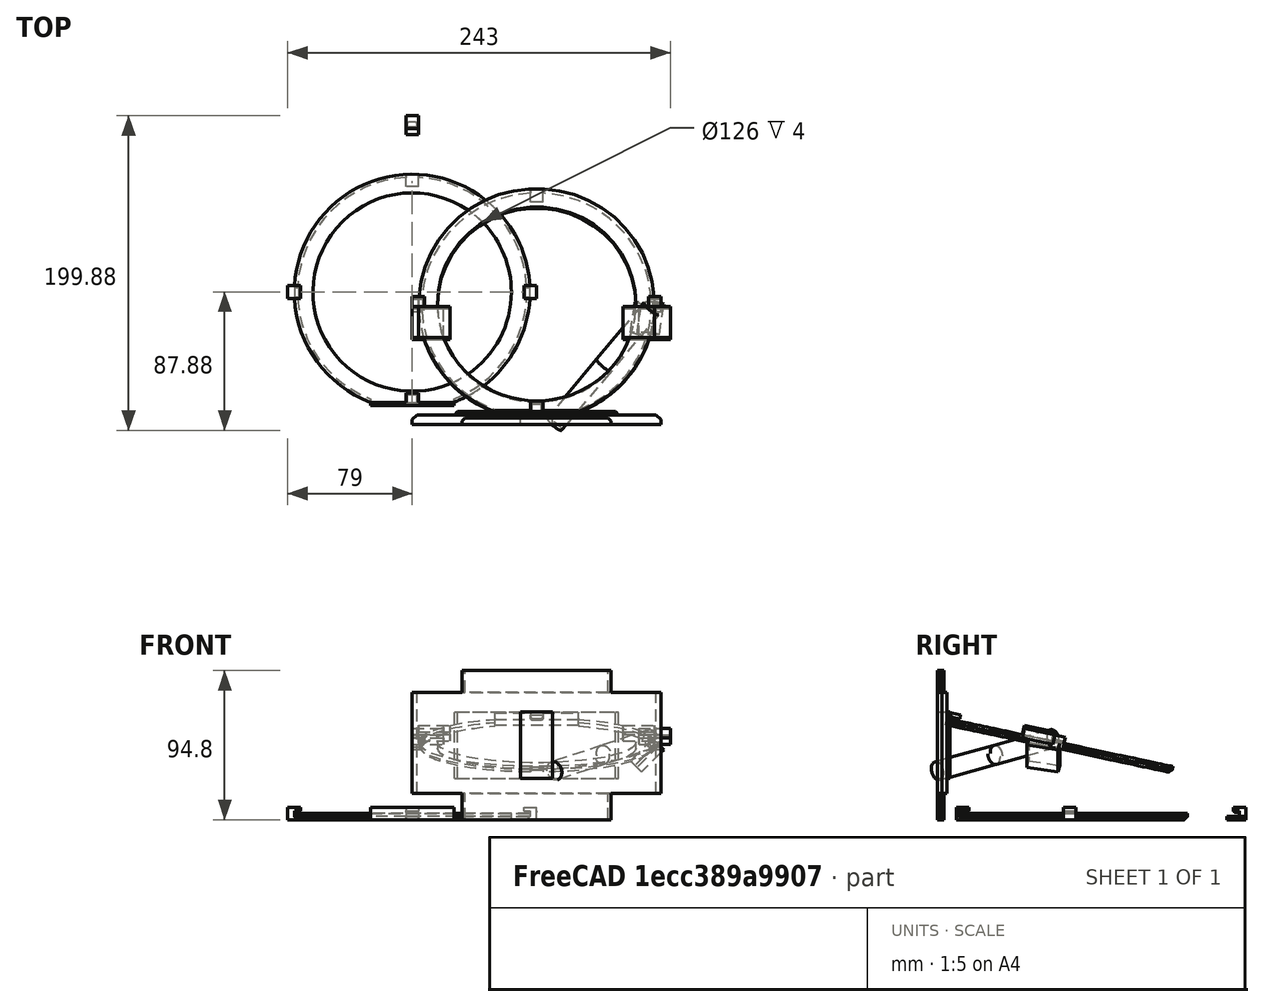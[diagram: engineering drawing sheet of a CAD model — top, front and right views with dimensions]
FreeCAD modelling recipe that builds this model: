
FCSTD DOCUMENT  (FreeCAD 0.19R0.19.2)
Label: waferHolder_021
License: All rights reserved
LicenseURL: http://en.wikipedia.org/wiki/All_rights_reserved
objects: Part::Box×48, Part::Chamfer×36, Part::MultiFuse×15, Part::Cut×12, Sketcher::SketchObject×9, Part::Extrusion×9, Part::Cylinder×8, Part::Fuse×2, Part::Mirroring×2, App::MeasureDistance×1
note: 141 computed .brp shape members not serialized (recipe doc carries the construction recipe); baked Part::Feature solids carry a one-line shape summary decoded from their .brp

FEATURE [Part::Box] Box003  label="bitHolderTop"
  AttacherType = Attacher::AttachEngine3D
  Height = 2
  Length = 8
  Placement = pos=(-4,100,0) rot=(0,0,1;0rad)
  Width = 12
FEATURE [Part::Box] Box008  label="holderBitLeft003"
  AttacherType = Attacher::AttachEngine3D
  Height = 2
  Length = 8
  Placement = pos=(-4,71,2) rot=(0,0,1;0rad)
  Width = 8
FEATURE [Part::Box] Box009  label="bitHolderTopCutout001"
  AttacherType = Attacher::AttachEngine3D
  Height = 4
  Length = 8
  Placement = pos=(-4,67,-2) rot=(0,0,1;0rad)
  Width = 12
FEATURE [Sketcher::SketchObject] Sketch002
  FullyConstrained = true
  sketch-geometry (3):
    g0: Circle CenterX=-3.1415e-12 CenterY=5.6243e-12 CenterZ=0 NormalX=0 NormalY=0 NormalZ=1 AngleXU=0 Radius=63
    g1: ArcOfCircle CenterX=-3.1415e-12 CenterY=5.6243e-12 CenterZ=0 NormalX=0 NormalY=0 NormalZ=1 AngleXU=0 Radius=74.8482 StartAngle=5.07429 EndAngle=10.6337
    g2: LineSegment StartX=-26.5 StartY=-70.0001 StartZ=0 EndX=26.5 EndY=-70.0001 EndZ=0
  constraints (6):
    c: Block(g0)
    c: Coincident(g1,g0)
    c: Block(g1)
    c: Coincident(g2,g1)
    c: Coincident(g2,g1)
    c: Horizontal(g2)
FEATURE [Part::Extrusion] Extrude002  label="mainHolderRing003"
  Base = -> Sketch002
  Dir = (0,0,1)
  DirMode = 2
  FaceMakerClass = Part::FaceMakerBullseye
  LengthFwd = 4
  LengthRev = 0
  Solid = true
  Symmetric = false
FEATURE [Part::Chamfer] Chamfer001
  Base = -> Extrude002
  Edges = 1 edges r=2: [Edge3]
FEATURE [Part::Cut] Cut002  label="mainHolderRing004"
  Base = -> Chamfer001
  Tool = -> Box009
FEATURE [Part::Cut] Cut003  label="bitHolderTop001"
  Base = -> Box008
  Tool = -> Cut002
FEATURE [Part::Box] Box010  label="holderBitLeft004"
  AttacherType = Attacher::AttachEngine3D
  Height = 2
  Length = 8
  Placement = pos=(-4,71,2) rot=(0,0,1;0rad)
  Width = 8
FEATURE [Part::Box] Box011  label="bitHolderTopCutout002"
  AttacherType = Attacher::AttachEngine3D
  Height = 4
  Length = 8
  Placement = pos=(-4,67,-2) rot=(0,0,1;0rad)
  Width = 12
FEATURE [Sketcher::SketchObject] Sketch003
  FullyConstrained = true
  sketch-geometry (3):
    g0: Circle CenterX=-3.1415e-12 CenterY=5.6243e-12 CenterZ=0 NormalX=0 NormalY=0 NormalZ=1 AngleXU=0 Radius=63
    g1: ArcOfCircle CenterX=-3.1415e-12 CenterY=5.6243e-12 CenterZ=0 NormalX=0 NormalY=0 NormalZ=1 AngleXU=0 Radius=74.8482 StartAngle=5.07429 EndAngle=10.6337
    g2: LineSegment StartX=-26.5 StartY=-70.0001 StartZ=0 EndX=26.5 EndY=-70.0001 EndZ=0
  constraints (6):
    c: Block(g0)
    c: Coincident(g1,g0)
    c: Block(g1)
    c: Coincident(g2,g1)
    c: Coincident(g2,g1)
    c: Horizontal(g2)
FEATURE [Part::Extrusion] Extrude003  label="mainHolderRing006"
  Base = -> Sketch003
  Dir = (0,0,1)
  DirMode = 2
  FaceMakerClass = Part::FaceMakerBullseye
  LengthFwd = 4
  LengthRev = 0
  Solid = true
  Symmetric = false
FEATURE [Part::Chamfer] Chamfer002
  Base = -> Extrude003
  Edges = 1 edges r=2: [Edge3]
FEATURE [Part::Cut] Cut005  label="mainHolderRing005"
  Base = -> Chamfer002
  Tool = -> Box011
FEATURE [Part::Cut] Cut004  label="bitHolderTop002"
  Base = -> Box010
  Placement = pos=(0,0,2) rot=(0,0,1;0rad)
  Tool = -> Cut005
FEATURE [Part::Box] Box012  label="holderBitLeft005"
  AttacherType = Attacher::AttachEngine3D
  Height = 2
  Length = 8
  Placement = pos=(-4,71,2) rot=(0,0,1;0rad)
  Width = 8
FEATURE [Part::Box] Box013  label="bitHolderTopCutout003"
  AttacherType = Attacher::AttachEngine3D
  Height = 4
  Length = 8
  Placement = pos=(-4,67,-2) rot=(0,0,1;0rad)
  Width = 12
FEATURE [Sketcher::SketchObject] Sketch004
  FullyConstrained = true
  sketch-geometry (3):
    g0: Circle CenterX=-3.1415e-12 CenterY=5.6243e-12 CenterZ=0 NormalX=0 NormalY=0 NormalZ=1 AngleXU=0 Radius=63
    g1: ArcOfCircle CenterX=-3.1415e-12 CenterY=5.6243e-12 CenterZ=0 NormalX=0 NormalY=0 NormalZ=1 AngleXU=0 Radius=74.8482 StartAngle=5.07429 EndAngle=10.6337
    g2: LineSegment StartX=-26.5 StartY=-70.0001 StartZ=0 EndX=26.5 EndY=-70.0001 EndZ=0
  constraints (6):
    c: Block(g0)
    c: Coincident(g1,g0)
    c: Block(g1)
    c: Coincident(g2,g1)
    c: Coincident(g2,g1)
    c: Horizontal(g2)
FEATURE [Part::Extrusion] Extrude004  label="mainHolderRing008"
  Base = -> Sketch004
  Dir = (0,0,1)
  DirMode = 2
  FaceMakerClass = Part::FaceMakerBullseye
  LengthFwd = 4
  LengthRev = 0
  Solid = true
  Symmetric = false
FEATURE [Part::Chamfer] Chamfer003
  Base = -> Extrude004
  Edges = 1 edges r=2: [Edge3]
FEATURE [Part::Cut] Cut007  label="mainHolderRing007"
  Base = -> Chamfer003
  Tool = -> Box013
FEATURE [Part::Cut] Cut006  label="bitHolderTop003"
  Base = -> Box012
  Placement = pos=(0,0,4) rot=(0,0,1;0rad)
  Tool = -> Cut007
FEATURE [Part::Box] Box014  label="bitHoldertop006"
  AttacherType = Attacher::AttachEngine3D
  Height = 3.4
  Length = 8
  Placement = pos=(-4,71,4.6) rot=(0,0,1;0rad)
  Width = 8
FEATURE [Part::MultiFuse] Fusion001  label="holderTop"
  Placement = pos=(0,33,0) rot=(0,0,1;0rad)
  Shapes = -> [Cut003,Cut004,Cut006,Box014]
FEATURE [Part::Chamfer] Chamfer004
  Base = -> Fusion001
  Edges = 1 edges r=1: [Edge16]
FEATURE [Part::Chamfer] Chamfer009
  Base = -> Chamfer004
  Edges = 1 edges r=1: [Edge1]
FEATURE [Part::Chamfer] Chamfer010
  Base = -> Chamfer009
  Edges = 1 edges r=1: [Edge32]
FEATURE [Part::Box] Box018  label="base001"
  AttacherType = Attacher::AttachEngine3D
  Height = 64.44
  Length = 158
  Placement = pos=(0,-84,16.6) rot=(0,0,1;0rad)
  Width = 6
FEATURE [Part::Box] Box019  label="base002"
  AttacherType = Attacher::AttachEngine3D
  Height = 94.8
  Length = 94.8
  Placement = pos=(31.6,-84,0) rot=(0,0,1;0rad)
  Width = 4
FEATURE [Part::Box] Box020  label="base003"
  AttacherType = Attacher::AttachEngine3D
  Height = 42.44
  Length = 104.28
  Placement = pos=(26.86,-84,26.18) rot=(0,0,1;0rad)
  Width = 8
FEATURE [Part::Chamfer] Chamfer014
  Base = -> Box018
  Edges = 1 edges r=3: [Edge3]
FEATURE [Part::Chamfer] Chamfer015
  Base = -> Chamfer014
  Edges = 1 edges r=3: [Edge15]
FEATURE [Part::Chamfer] Chamfer016
  Base = -> Box019
  Edges = 1 edges r=2: [Edge3]
FEATURE [Part::Chamfer] Chamfer017
  Base = -> Box020
  Edges = 1 edges r=2: [Edge3]
FEATURE [Part::Chamfer] Chamfer018
  Base = -> Chamfer016
  Edges = 1 edges r=2: [Edge15]
FEATURE [Part::Chamfer] Chamfer019
  Base = -> Chamfer017
  Edges = 1 edges r=2: [Edge15]
FEATURE [Part::MultiFuse] Fusion002  label="base004"
  Shapes = -> [Chamfer015,Chamfer018,Chamfer019]
FEATURE [Part::Box] Box021  label="holderBitLeft006"
  AttacherType = Attacher::AttachEngine3D
  Height = 4
  Length = 6
  Placement = pos=(-79,-4,0) rot=(0,0,1;0rad)
  Width = 8
FEATURE [Part::Box] Box022  label="holderBitright003"
  AttacherType = Attacher::AttachEngine3D
  Height = 4
  Length = 6
  Placement = pos=(73,-4,0) rot=(0,0,1;0rad)
  Width = 8
FEATURE [Part::Box] Box023  label="holderBitLeft007"
  AttacherType = Attacher::AttachEngine3D
  Height = 3.4
  Length = 8
  Placement = pos=(-79,-4,4.6) rot=(0,0,1;0rad)
  Width = 8
FEATURE [Part::Box] Box024  label="holderBitRight003"
  AttacherType = Attacher::AttachEngine3D
  Height = 3.4
  Length = 8
  Placement = pos=(71,-4,4.6) rot=(0,0,1;0rad)
  Width = 8
FEATURE [Sketcher::SketchObject] Sketch005
  FullyConstrained = true
  sketch-geometry (3):
    g0: Circle CenterX=-3.1415e-12 CenterY=5.6243e-12 CenterZ=0 NormalX=0 NormalY=0 NormalZ=1 AngleXU=0 Radius=63
    g1: ArcOfCircle CenterX=-3.1415e-12 CenterY=5.6243e-12 CenterZ=0 NormalX=0 NormalY=0 NormalZ=1 AngleXU=0 Radius=74.8482 StartAngle=5.07429 EndAngle=10.6337
    g2: LineSegment StartX=-26.5 StartY=-70.0001 StartZ=0 EndX=26.5 EndY=-70.0001 EndZ=0
  constraints (6):
    c: Block(g0)
    c: Coincident(g1,g0)
    c: Block(g1)
    c: Coincident(g2,g1)
    c: Coincident(g2,g1)
    c: Horizontal(g2)
FEATURE [Part::Box] Box025  label="holderBitLeft008"
  AttacherType = Attacher::AttachEngine3D
  Height = 4
  Length = 8
  Placement = pos=(-79,-4,0) rot=(0,0,1;0rad)
  Width = 8
FEATURE [Part::Box] Box026  label="bitHolderTopCutout004"
  AttacherType = Attacher::AttachEngine3D
  Height = 4
  Length = 8
  Placement = pos=(-4,67,-2) rot=(0,0,1;0rad)
  Width = 12
FEATURE [Part::Extrusion] Extrude006  label="mainHolderRing010"
  Base = -> Sketch005
  Dir = (0,0,1)
  DirMode = 2
  FaceMakerClass = Part::FaceMakerBullseye
  LengthFwd = 4
  LengthRev = 0
  Solid = true
  Symmetric = false
FEATURE [Part::Box] Box027  label="holderBitRight004"
  AttacherType = Attacher::AttachEngine3D
  Height = 4
  Length = 8
  Placement = pos=(71,-4,0) rot=(0,0,1;0rad)
  Width = 8
FEATURE [Part::Chamfer] Chamfer020
  Base = -> Extrude006
  Edges = 1 edges r=2: [Edge3]
FEATURE [Part::Cut] Cut008  label="mainHolderRing011"
  Base = -> Chamfer020
  Tool = -> Box026
FEATURE [Part::MultiFuse] Fusion004  label="holders001"
  Shapes = -> [Box021,Box022]
FEATURE [Sketcher::SketchObject] Sketch006
  FullyConstrained = true
  sketch-geometry (3):
    g0: Circle CenterX=-3.1415e-12 CenterY=5.6243e-12 CenterZ=0 NormalX=0 NormalY=0 NormalZ=1 AngleXU=0 Radius=63
    g1: ArcOfCircle CenterX=-3.1415e-12 CenterY=5.6243e-12 CenterZ=0 NormalX=0 NormalY=0 NormalZ=1 AngleXU=0 Radius=74.8482 StartAngle=5.07429 EndAngle=10.6337
    g2: LineSegment StartX=-26.5 StartY=-70.0001 StartZ=0 EndX=26.5 EndY=-70.0001 EndZ=0
  constraints (6):
    c: Block(g0)
    c: Coincident(g1,g0)
    c: Block(g1)
    c: Coincident(g2,g1)
    c: Coincident(g2,g1)
    c: Horizontal(g2)
FEATURE [Part::Extrusion] Extrude005  label="mainHolderRing009"
  Base = -> Sketch006
  Dir = (0,0,1)
  DirMode = 2
  FaceMakerClass = Part::FaceMakerBullseye
  LengthFwd = 4
  LengthRev = 0
  Solid = true
  Symmetric = false
FEATURE [Part::Cut] Cut009  label="leftAndRightHolderBits001"
  Base = -> Fusion004
  Placement = pos=(0,0,4) rot=(0,0,1;0rad)
  Tool = -> Extrude005
FEATURE [Part::Chamfer] Chamfer021
  Base = -> Box023
  Edges = 1 edges r=1: [Edge8]
FEATURE [Part::Chamfer] Chamfer022
  Base = -> Box024
  Edges = 1 edges r=1: [Edge4]
FEATURE [Part::Chamfer] Chamfer023
  Base = -> Chamfer022
  Edges = 1 edges r=1: [Edge13]
FEATURE [Part::Chamfer] Chamfer024
  Base = -> Chamfer023
  Edges = 1 edges r=1: [Edge5]
FEATURE [Part::Box] Box028  label="holderBottom004"
  AttacherType = Attacher::AttachEngine3D
  Height = 4
  Length = 53
  Placement = pos=(-26.5,-72,0) rot=(0,0,1;0rad)
  Width = 4.5
FEATURE [Part::Chamfer] Chamfer025
  Base = -> Chamfer021
  Edges = 1 edges r=1: [Edge5]
FEATURE [Part::Chamfer] Chamfer026
  Base = -> Chamfer025
  Edges = 1 edges r=1: [Edge16]
FEATURE [Part::Box] Box029  label="holderBottom006"
  AttacherType = Attacher::AttachEngine3D
  Height = 4
  Length = 53
  Placement = pos=(-26.5,-72,4) rot=(0,0,1;0rad)
  Width = 2
FEATURE [Part::Box] Box030  label="holderBottom007"
  AttacherType = Attacher::AttachEngine3D
  Height = 3.4
  Length = 8
  Placement = pos=(-4,-72,4.6) rot=(0,0,1;0rad)
  Width = 8
FEATURE [Part::Chamfer] Chamfer027  label="holderBottom005"
  Base = -> Box030
  Edges = 3 edges r=1: [Edge4,Edge8,Edge11]
FEATURE [Part::MultiFuse] Fusion005  label="removeRingHolder"
  Placement = pos=(79,-8.35,45.4) rot=(1,0,0;6.07375rad)
  Shapes = -> [Box025,Box027,Cut008,Cut009,Chamfer024,Chamfer026,Box028,Box029,Chamfer027]
FEATURE [Part::Box] Box017  label="holderBottom002"
  AttacherType = Attacher::AttachEngine3D
  Height = 3.4
  Length = 8
  Placement = pos=(-4,-72,4.6) rot=(0,0,1;0rad)
  Width = 8
FEATURE [Part::Chamfer] Chamfer013  label="holderBottom003"
  Base = -> Box017
  Edges = 3 edges r=1: [Edge4,Edge8,Edge11]
FEATURE [Part::Box] Box016  label="holderBottom001"
  AttacherType = Attacher::AttachEngine3D
  Height = 4
  Length = 53
  Placement = pos=(-26.5,-72,4) rot=(0,0,1;0rad)
  Width = 2
FEATURE [Part::Box] Box015  label="holderBottom"
  AttacherType = Attacher::AttachEngine3D
  Height = 4
  Length = 53
  Placement = pos=(-26.5,-72,0) rot=(0,0,1;0rad)
  Width = 4.5
FEATURE [Part::Box] Box006  label="holderBitLeft002"
  AttacherType = Attacher::AttachEngine3D
  Height = 3.4
  Length = 8
  Placement = pos=(-79,-4,4.6) rot=(0,0,1;0rad)
  Width = 8
FEATURE [Part::Chamfer] Chamfer005
  Base = -> Box006
  Edges = 1 edges r=1: [Edge8]
FEATURE [Part::Chamfer] Chamfer011
  Base = -> Chamfer005
  Edges = 1 edges r=1: [Edge5]
FEATURE [Part::Chamfer] Chamfer012
  Base = -> Chamfer011
  Edges = 1 edges r=1: [Edge16]
FEATURE [Part::Box] Box007  label="holderBitRight002"
  AttacherType = Attacher::AttachEngine3D
  Height = 3.4
  Length = 8
  Placement = pos=(71,-4,4.6) rot=(0,0,1;0rad)
  Width = 8
FEATURE [Part::Chamfer] Chamfer006
  Base = -> Box007
  Edges = 1 edges r=1: [Edge4]
FEATURE [Part::Chamfer] Chamfer007
  Base = -> Chamfer006
  Edges = 1 edges r=1: [Edge13]
FEATURE [Part::Chamfer] Chamfer008
  Base = -> Chamfer007
  Edges = 1 edges r=1: [Edge5]
FEATURE [Sketcher::SketchObject] Sketch001
  FullyConstrained = true
  sketch-geometry (3):
    g0: Circle CenterX=-3.1415e-12 CenterY=5.6243e-12 CenterZ=0 NormalX=0 NormalY=0 NormalZ=1 AngleXU=0 Radius=63
    g1: ArcOfCircle CenterX=-3.1415e-12 CenterY=5.6243e-12 CenterZ=0 NormalX=0 NormalY=0 NormalZ=1 AngleXU=0 Radius=74.8482 StartAngle=5.07429 EndAngle=10.6337
    g2: LineSegment StartX=-26.5 StartY=-70.0001 StartZ=0 EndX=26.5 EndY=-70.0001 EndZ=0
  constraints (6):
    c: Block(g0)
    c: Coincident(g1,g0)
    c: Block(g1)
    c: Coincident(g2,g1)
    c: Coincident(g2,g1)
    c: Horizontal(g2)
FEATURE [Part::Extrusion] Extrude001  label="mainHolderRing002"
  Base = -> Sketch001
  Dir = (0,0,1)
  DirMode = 2
  FaceMakerClass = Part::FaceMakerBullseye
  LengthFwd = 4
  LengthRev = 0
  Solid = true
  Symmetric = false
FEATURE [Part::Box] Box005  label="holderBitright002"
  AttacherType = Attacher::AttachEngine3D
  Height = 4
  Length = 6
  Placement = pos=(73,-4,0) rot=(0,0,1;0rad)
  Width = 8
FEATURE [Part::Box] Box004  label="holderBitLeft001"
  AttacherType = Attacher::AttachEngine3D
  Height = 4
  Length = 6
  Placement = pos=(-79,-4,0) rot=(0,0,1;0rad)
  Width = 8
FEATURE [Part::MultiFuse] Fusion  label="holders"
  Shapes = -> [Box004,Box005]
FEATURE [Part::Cut] Cut001  label="leftAndRightHolderBits"
  Base = -> Fusion
  Placement = pos=(0,0,4) rot=(0,0,1;0rad)
  Tool = -> Extrude001
FEATURE [Part::Box] Box001  label="bitHolderTopCutout"
  AttacherType = Attacher::AttachEngine3D
  Height = 4
  Length = 8
  Placement = pos=(-4,67,-2) rot=(0,0,1;0rad)
  Width = 12
FEATURE [Sketcher::SketchObject] Sketch
  FullyConstrained = true
  sketch-geometry (3):
    g0: Circle CenterX=-3.1415e-12 CenterY=5.6243e-12 CenterZ=0 NormalX=0 NormalY=0 NormalZ=1 AngleXU=0 Radius=63
    g1: ArcOfCircle CenterX=-3.1415e-12 CenterY=5.6243e-12 CenterZ=0 NormalX=0 NormalY=0 NormalZ=1 AngleXU=0 Radius=74.8482 StartAngle=5.07429 EndAngle=10.6337
    g2: LineSegment StartX=-26.5 StartY=-70.0001 StartZ=0 EndX=26.5 EndY=-70.0001 EndZ=0
  constraints (6):
    c: Block(g0)
    c: Coincident(g1,g0)
    c: Block(g1)
    c: Coincident(g2,g1)
    c: Coincident(g2,g1)
    c: Horizontal(g2)
FEATURE [Part::Extrusion] Extrude  label="mainHolderRing"
  Base = -> Sketch
  Dir = (0,0,1)
  DirMode = 2
  FaceMakerClass = Part::FaceMakerBullseye
  LengthFwd = 4
  LengthRev = 0
  Solid = true
  Symmetric = false
FEATURE [Part::Chamfer] Chamfer
  Base = -> Extrude
  Edges = 1 edges r=2: [Edge3]
FEATURE [Part::Cut] Cut  label="mainHolderRing001"
  Base = -> Chamfer
  Tool = -> Box001
FEATURE [Part::Box] Box002  label="holderBitRight"
  AttacherType = Attacher::AttachEngine3D
  Height = 4
  Length = 8
  Placement = pos=(71,-4,0) rot=(0,0,1;0rad)
  Width = 8
FEATURE [Part::Box] Box  label="holderBitLeft"
  AttacherType = Attacher::AttachEngine3D
  Height = 4
  Length = 8
  Placement = pos=(-79,-4,0) rot=(0,0,1;0rad)
  Width = 8
FEATURE [Part::MultiFuse] Fusion003  label="ringHolder"
  Shapes = -> [Box,Box002,Cut,Cut001,Chamfer008,Chamfer012,Box015,Box016,Chamfer013]
FEATURE [Part::Cylinder] Cylinder
  Angle = 360
  AttacherType = Attacher::AttachEngine3D
  Height = 50
  Placement = pos=(34.86,-30,47.4) rot=(1,0,0;1.5708rad)
  Radius = 6
FEATURE [Part::Box] Box031  label="base005"
  AttacherType = Attacher::AttachEngine3D
  Height = 42.44
  Length = 20.28
  Placement = pos=(68.86,-84,26.18) rot=(0,0,1;0rad)
  Width = 8
FEATURE [Part::Cylinder] Cylinder001
  Angle = 360
  AttacherType = Attacher::AttachEngine3D
  Height = 50
  Placement = pos=(34.86,-30,47.4) rot=(1,0,0;1.5708rad)
  Radius = 6
FEATURE [Part::MultiFuse] Fusion006
  Placement = pos=(0,0,0) rot=(1,0,0;0.20944rad)
  Shapes = -> [Cylinder001,Cylinder]
FEATURE [Part::Cylinder] Cylinder002
  Angle = 360
  AttacherType = Attacher::AttachEngine3D
  Height = 50
  Placement = pos=(34.86,-30,47.4) rot=(1,0,0;1.5708rad)
  Radius = 6
FEATURE [Part::Cylinder] Cylinder003
  Angle = 360
  AttacherType = Attacher::AttachEngine3D
  Height = 50
  Placement = pos=(34.86,-30,47.4) rot=(1,0,0;1.5708rad)
  Radius = 6
FEATURE [Part::MultiFuse] Fusion007
  Placement = pos=(0,0,0) rot=(1,0,0;0.20944rad)
  Shapes = -> [Cylinder003,Cylinder002]
FEATURE [Part::MultiFuse] Fusion008
  Placement = pos=(-44.06,-5,11.27) rot=(0,0,1;0.698132rad)
  Shapes = -> [Fusion007,Fusion006]
FEATURE [App::MeasureDistance] Distance  label="Distance: 0.65 mm"
  Distance = 0.654413
  P1 = (68.86,-76,67.959)
  P2 = (68.8586,-76,68.6134)
FEATURE [Part::Cylinder] Cylinder004
  Angle = 360
  AttacherType = Attacher::AttachEngine3D
  Height = 50
  Placement = pos=(34.86,-30,47.4) rot=(1,0,0;1.5708rad)
  Radius = 6
FEATURE [Part::Cylinder] Cylinder005
  Angle = 360
  AttacherType = Attacher::AttachEngine3D
  Height = 50
  Placement = pos=(34.86,-30,47.4) rot=(1,0,0;1.5708rad)
  Radius = 6
FEATURE [Part::MultiFuse] Fusion010
  Placement = pos=(0,0,0) rot=(1,0,0;0.20944rad)
  Shapes = -> [Cylinder005,Cylinder004]
FEATURE [Part::Cylinder] Cylinder006
  Angle = 360
  AttacherType = Attacher::AttachEngine3D
  Height = 50
  Placement = pos=(34.86,-30,47.4) rot=(1,0,0;1.5708rad)
  Radius = 6
FEATURE [Part::Cylinder] Cylinder007
  Angle = 360
  AttacherType = Attacher::AttachEngine3D
  Height = 50
  Placement = pos=(34.86,-30,47.4) rot=(1,0,0;1.5708rad)
  Radius = 6
FEATURE [Part::MultiFuse] Fusion009
  Placement = pos=(0,0,0) rot=(1,0,0;0.20944rad)
  Shapes = -> [Cylinder007,Cylinder006]
FEATURE [Part::MultiFuse] Fusion011
  Placement = pos=(-14,-40.82,1.35) rot=(0,0,1;0.698132rad)
  Shapes = -> [Fusion009,Fusion010]
FEATURE [Part::Fuse] Fusion012
  Base = -> Fusion008
  Placement = pos=(-1.7,2,0) rot=(0,0,1;0rad)
  Tool = -> Fusion011
FEATURE [Part::Mirroring] Part__Mirroring  label="Fusion012 (Mirror #1)"
  Base = (0,0,0)
  Normal = (1,0,0)
  Placement = pos=(158,0,0) rot=(0,0,1;0rad)
  Source = -> Fusion012
FEATURE [Part::Box] Box032  label="removeStrutLeft"
  AttacherType = Attacher::AttachEngine3D
  Height = 6
  Length = 20
  Placement = pos=(4,-30.1,54.1) rot=(1,0,0;6.07375rad)
  Width = 20
FEATURE [Part::Box] Box033  label="reoveStrustRight"
  AttacherType = Attacher::AttachEngine3D
  Height = 6
  Length = 20
  Placement = pos=(134,-30.1,54.1) rot=(-1,0,0;0.20944rad)
  Width = 20
FEATURE [Part::Box] Box034  label="removeStrutLeft001"
  AttacherType = Attacher::AttachEngine3D
  Height = 6
  Length = 20
  Placement = pos=(4,-30.1,54.1) rot=(-1,0,0;0.20944rad)
  Width = 20
FEATURE [Part::Box] Box035  label="removeStrutLeft002"
  AttacherType = Attacher::AttachEngine3D
  Height = 6
  Length = 20
  Placement = pos=(4,-30.1,54.1) rot=(-1,0,0;0.20944rad)
  Width = 20
FEATURE [Part::Fuse] Fusion013
  Base = -> Box034
  Placement = pos=(-40,3,12) rot=(0,1,0;0.785398rad)
  Tool = -> Box035
FEATURE [Part::Mirroring] Part__Mirroring001  label="Fusion013 (Mirror #2)"
  Base = (0,0,0)
  Normal = (1,0,0)
  Placement = pos=(158,0,0) rot=(0,0,1;0rad)
  Source = -> Fusion013
FEATURE [Part::Box] Box036  label="reoveStrustRight001"
  AttacherType = Attacher::AttachEngine3D
  Height = 6
  Length = 20
  Placement = pos=(144,-30.1,52.1) rot=(-1,0,0;0.20944rad)
  Width = 20
FEATURE [Part::Box] Box037  label="reoveStrustLeft002"
  AttacherType = Attacher::AttachEngine3D
  Height = 6
  Length = 20
  Placement = pos=(0,-30.1,52.1) rot=(-1,0,0;0.20944rad)
  Width = 20
FEATURE [Sketcher::SketchObject] Sketch007
  FullyConstrained = true
  sketch-geometry (3):
    g0: Circle CenterX=-3.1415e-12 CenterY=5.6243e-12 CenterZ=0 NormalX=0 NormalY=0 NormalZ=1 AngleXU=0 Radius=63
    g1: ArcOfCircle CenterX=-3.1415e-12 CenterY=5.6243e-12 CenterZ=0 NormalX=0 NormalY=0 NormalZ=1 AngleXU=0 Radius=74.8482 StartAngle=5.07429 EndAngle=10.6337
    g2: LineSegment StartX=-26.5 StartY=-70.0001 StartZ=0 EndX=26.5 EndY=-70.0001 EndZ=0
  constraints (6):
    c: Block(g0)
    c: Coincident(g1,g0)
    c: Block(g1)
    c: Coincident(g2,g1)
    c: Coincident(g2,g1)
    c: Horizontal(g2)
FEATURE [Part::Box] Box038  label="holderBitLeft009"
  AttacherType = Attacher::AttachEngine3D
  Height = 4
  Length = 6
  Placement = pos=(-79,-4,0) rot=(0,0,1;0rad)
  Width = 8
FEATURE [Part::Box] Box039  label="holderBitright004"
  AttacherType = Attacher::AttachEngine3D
  Height = 4
  Length = 6
  Placement = pos=(73,-4,0) rot=(0,0,1;0rad)
  Width = 8
FEATURE [Part::Box] Box040  label="holderBitLeft010"
  AttacherType = Attacher::AttachEngine3D
  Height = 3.4
  Length = 8
  Placement = pos=(-79,-4,4.6) rot=(0,0,1;0rad)
  Width = 8
FEATURE [Part::Box] Box041  label="holderBitRight005"
  AttacherType = Attacher::AttachEngine3D
  Height = 3.4
  Length = 8
  Placement = pos=(71,-4,4.6) rot=(0,0,1;0rad)
  Width = 8
FEATURE [Part::Extrusion] Extrude008  label="mainHolderRing013"
  Base = -> Sketch007
  Dir = (0,0,1)
  DirMode = 2
  FaceMakerClass = Part::FaceMakerBullseye
  LengthFwd = 4
  LengthRev = 0
  Solid = true
  Symmetric = false
FEATURE [Part::Box] Box042  label="holderBitRight006"
  AttacherType = Attacher::AttachEngine3D
  Height = 4
  Length = 8
  Placement = pos=(71,-4,0) rot=(0,0,1;0rad)
  Width = 8
FEATURE [Part::Box] Box043  label="holderBottom008"
  AttacherType = Attacher::AttachEngine3D
  Height = 4
  Length = 53
  Placement = pos=(-26.5,-72,0) rot=(0,0,1;0rad)
  Width = 4.5
FEATURE [Part::Box] Box044  label="holderBottom009"
  AttacherType = Attacher::AttachEngine3D
  Height = 4
  Length = 53
  Placement = pos=(-26.5,-72,4) rot=(0,0,1;0rad)
  Width = 2
FEATURE [Part::Box] Box045  label="holderBottom010"
  AttacherType = Attacher::AttachEngine3D
  Height = 3.4
  Length = 8
  Placement = pos=(-4,-72,4.6) rot=(0,0,1;0rad)
  Width = 8
FEATURE [Part::Box] Box046  label="holderBitLeft011"
  AttacherType = Attacher::AttachEngine3D
  Height = 4
  Length = 8
  Placement = pos=(-79,-4,0) rot=(0,0,1;0rad)
  Width = 8
FEATURE [Part::Box] Box047  label="bitHolderTopCutout005"
  AttacherType = Attacher::AttachEngine3D
  Height = 4
  Length = 8
  Placement = pos=(-4,67,-2) rot=(0,0,1;0rad)
  Width = 12
FEATURE [Part::Chamfer] Chamfer031  label="holderBottom011"
  Base = -> Box045
  Edges = 3 edges r=1: [Edge4,Edge8,Edge11]
FEATURE [Sketcher::SketchObject] Sketch008
  FullyConstrained = true
  sketch-geometry (3):
    g0: Circle CenterX=-3.1415e-12 CenterY=5.6243e-12 CenterZ=0 NormalX=0 NormalY=0 NormalZ=1 AngleXU=0 Radius=63
    g1: ArcOfCircle CenterX=-3.1415e-12 CenterY=5.6243e-12 CenterZ=0 NormalX=0 NormalY=0 NormalZ=1 AngleXU=0 Radius=74.8482 StartAngle=5.07429 EndAngle=10.6337
    g2: LineSegment StartX=-26.5 StartY=-70.0001 StartZ=0 EndX=26.5 EndY=-70.0001 EndZ=0
  constraints (6):
    c: Block(g0)
    c: Coincident(g1,g0)
    c: Block(g1)
    c: Coincident(g2,g1)
    c: Coincident(g2,g1)
    c: Horizontal(g2)
FEATURE [Part::Extrusion] Extrude007  label="mainHolderRing012"
  Base = -> Sketch008
  Dir = (0,0,1)
  DirMode = 2
  FaceMakerClass = Part::FaceMakerBullseye
  LengthFwd = 4
  LengthRev = 0
  Solid = true
  Symmetric = false
FEATURE [Part::Chamfer] Chamfer032
  Base = -> Extrude008
  Edges = 1 edges r=2: [Edge3]
FEATURE [Part::Cut] Cut010  label="mainHolderRing014"
  Base = -> Chamfer032
  Tool = -> Box047
FEATURE [Part::MultiFuse] Fusion015  label="holders002"
  Shapes = -> [Box038,Box039]
FEATURE [Part::Cut] Cut011  label="leftAndRightHolderBits002"
  Base = -> Fusion015
  Placement = pos=(0,0,4) rot=(0,0,1;0rad)
  Tool = -> Extrude007
FEATURE [Part::Chamfer] Chamfer033
  Base = -> Box040
  Edges = 1 edges r=1: [Edge8]
FEATURE [Part::Chamfer] Chamfer029
  Base = -> Chamfer033
  Edges = 1 edges r=1: [Edge5]
FEATURE [Part::Chamfer] Chamfer030
  Base = -> Chamfer029
  Edges = 1 edges r=1: [Edge16]
FEATURE [Part::Chamfer] Chamfer034
  Base = -> Box041
  Edges = 1 edges r=1: [Edge4]
FEATURE [Part::Chamfer] Chamfer035
  Base = -> Chamfer034
  Edges = 1 edges r=1: [Edge13]
FEATURE [Part::Chamfer] Chamfer028
  Base = -> Chamfer035
  Edges = 1 edges r=1: [Edge5]
FEATURE [Part::MultiFuse] Fusion014  label="removeRingHolder001"
  Placement = pos=(79,-8.35,45.4) rot=(-1,0,0;0.20944rad)
  Shapes = -> [Box046,Box042,Cut010,Cut011,Chamfer028,Chamfer030,Box043,Box044,Chamfer031]
FEATURE [Part::MultiFuse] Fusion016  label="removeFromStruts"
  Shapes = -> [Box037,Box036]
